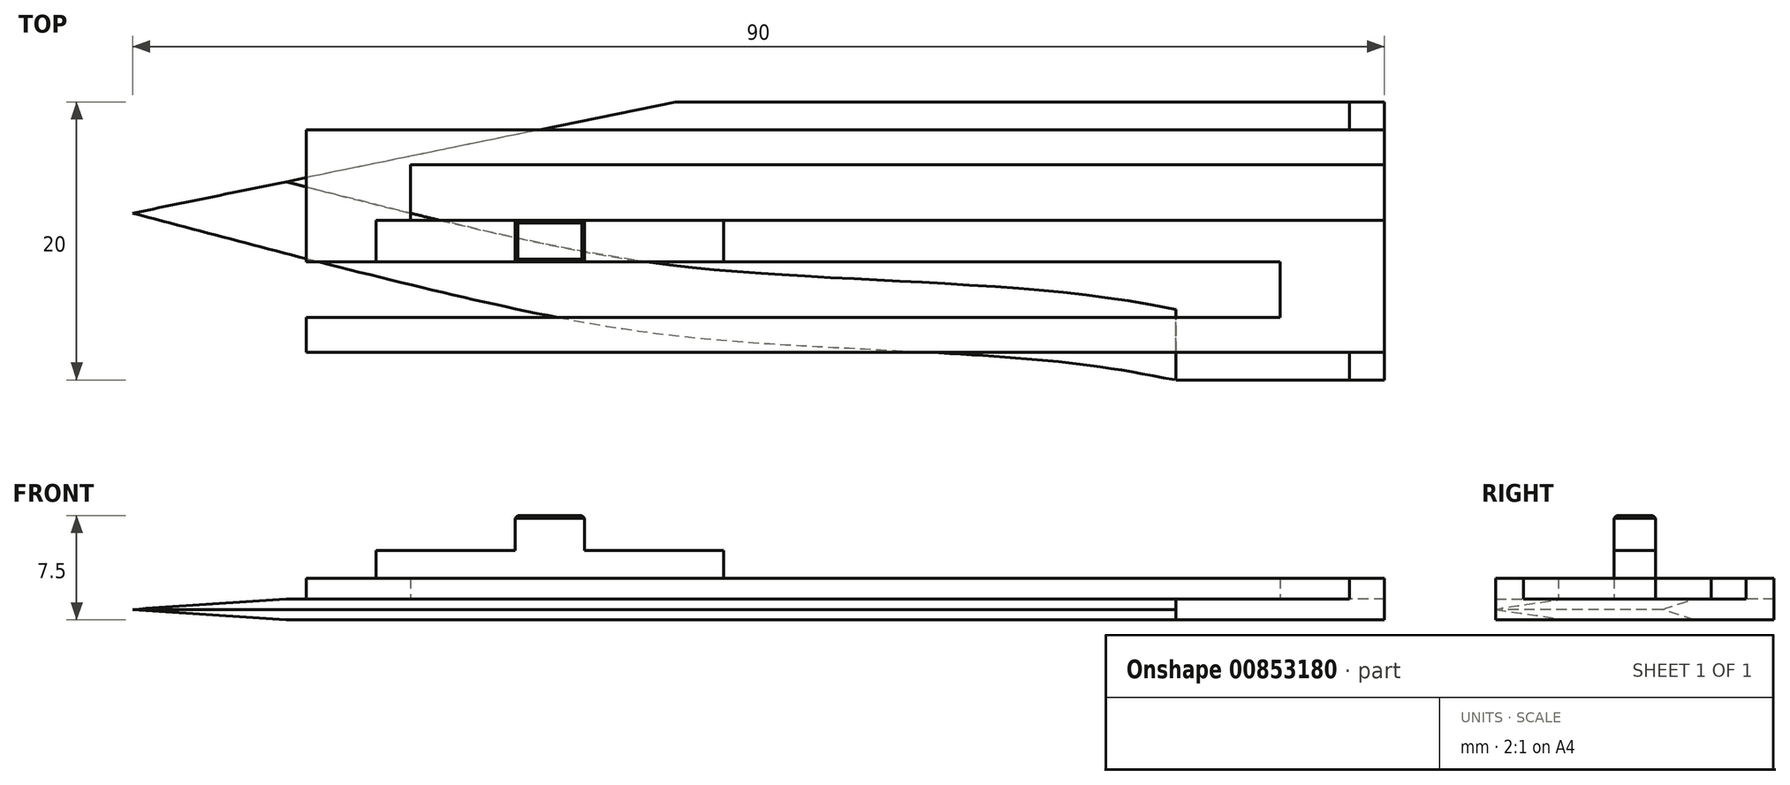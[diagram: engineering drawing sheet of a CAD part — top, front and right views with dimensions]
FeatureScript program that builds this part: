
annotation { "Feature Type Name" : "Feature", "Feature Type Description" : "" }
export const myFeature = defineFeature(function(context is Context, id is Id, definition is map)
    precondition{}
    {
        {
            var Q0;
            Q0=qCreatedBy(makeId("Top.planeOp"),FACE);
            var sketch = newSketch(context, id + "F0", { "sketchPlane" : qUnion([Q0])});
            skLineSegment(sketch, "E0.bottom", {"start": v(45, 10) * mm, "end": v(-5.97, 10) * mm});
            skLineSegment(sketch, "E0.left", {"start": v(45, 10) * mm, "end": v(45, -10) * mm});
            skPoint(sketch, "E0.middle", {"position": v(0, 0) * mm});
            skLineSegment(sketch, "E1", {"start": v(-5.97, 10) * mm, "end": v(-45, 2) * mm});
            skPoint(sketch, "E2.orphan", {"position": v(-45, 10) * mm});
            skPoint(sketch, "E0.top.end.orphan", {"position": v(-45, -10) * mm});
            skLineSegment(sketch, "E3", {"start": v(45, -10) * mm, "end": v(30, -10) * mm});
            skLineSegment(sketch, "E4", {"start": v(30, -10) * mm, "end": v(30, 10) * mm});
            skFitSpline(sketch, "E5", {"points": [v(-45, 2) * mm, v(-13.69, -5.63) * mm, v(2.33, -7.47) * mm, v(21.39, -8.67) * mm, v(30, -10) * mm], "startDerivative": vector(102.97, -27.22) * mm, "endDerivative": vector(43.54, -8.37) * mm});
            skSolve(sketch);
        }
        {
            var Q0;
            Q0 = qSketchRegion(id + "F0", true);
            extrude(context, id + "F1", {"entities" : qUnion([Q0]), "endBound" : BoundingType.SYMMETRIC, "depth" : 1.5 * mm, "offsetDistance" : 25 * mm});
        }
        {
            var Q0;
            Q0=makeQuery(id+"F1.opExtrude","CAP_EDGE",EDGE,{"disambiguationData":[OSD([sQuery(id+"F0.wireOp",EDGE,"E5")])],"isStart":false});
            var Q1;
            Q1=makeQuery(id+"F1.opExtrude","CAP_EDGE",EDGE,{"disambiguationData":[OSD([sQuery(id+"F0.wireOp",EDGE,"E5")])],"isStart":true});
            chamfer(context, id + "F2", {"entities" : qUnion([Q0, Q1]), "chamferType" : ChamferType.TWO_OFFSETS, "width1" : 5 * mm, "oppositeDirection" : false, "width2" : (1.5 / 2) * mm, "tangentPropagation" : true});
        }
        {
            var Q0;
            {var subQ0=sQuery(id+"F0.wireOp",EDGE,"E0.left");Q0=makeQuery(id+"F0.imprint","IMPRINT",FACE,{"disambiguationData":[TD([[makeQuery(id+"F0.imprint","IMPRINT",EDGE,{"derivedFrom":subQ0}),-1.0]])]});}
            extrude(context, id + "F3", {"entities" : qUnion([Q0]), "operationType" : NewBodyOperationType.ADD, "endBound" : BoundingType.SYMMETRIC, "depth" : 1.5 * mm, "offsetDistance" : 25 * mm});
        }
        {
            var Q0;
            {var subQ0=sQuery(id+"F0.wireOp",EDGE,"E3");var subQ1=sQuery(id+"F0.wireOp",EDGE,"E0.left");var subQ2=sQuery(id+"F0.wireOp",EDGE,"E0.bottom");Q0=makeQuery(id+"F3.boolean.opBoolean","MERGE",FACE,{"derivedFrom":[makeQuery(id+"F1.opExtrude","CAP_FACE",FACE,{"disambiguationData":[OSD([subQ2,subQ1,sQuery(id+"F0.wireOp",EDGE,"E1"),subQ0,sQuery(id+"F0.wireOp",EDGE,"E5")])],"isStart":false}),makeQuery(id+"F3.opExtrude","CAP_FACE",FACE,{"disambiguationData":[OSD([subQ2,subQ1,subQ0,sQuery(id+"F0.wireOp",EDGE,"E4")])],"isStart":false})]});}
            var sketch = newSketch(context, id + "F4", { "sketchPlane" : qUnion([Q0])});
            skLineSegment(sketch, "E6.bottom", {"start": v(45, -10) * mm, "end": v(42.5, -10) * mm});
            skLineSegment(sketch, "E6.top", {"start": v(45, -8) * mm, "end": v(42.5, -8) * mm});
            skLineSegment(sketch, "E6.left", {"start": v(45, -10) * mm, "end": v(45, -8) * mm});
            skLineSegment(sketch, "E6.right", {"start": v(42.5, -10) * mm, "end": v(42.5, -8) * mm});
            skLineSegment(sketch, "E7.bottom", {"start": v(45, 10) * mm, "end": v(42.5, 10) * mm});
            skLineSegment(sketch, "E7.top", {"start": v(45, 8) * mm, "end": v(42.5, 8) * mm});
            skLineSegment(sketch, "E7.left", {"start": v(45, 10) * mm, "end": v(45, 8) * mm});
            skLineSegment(sketch, "E7.right", {"start": v(42.5, 10) * mm, "end": v(42.5, 8) * mm});
            skSolve(sketch);
        }
        {
            var Q0;
            Q0 = qSketchRegion(id + "F4", true);
            extrude(context, id + "F5", {"entities" : qUnion([Q0]), "operationType" : NewBodyOperationType.ADD, "depth" : 1.5 * mm, "offsetDistance" : 25 * mm});
        }
        {
            var Q0;
            {var subQ0=sQuery(id+"F0.wireOp",EDGE,"E3");var subQ1=sQuery(id+"F0.wireOp",EDGE,"E0.left");var subQ2=sQuery(id+"F0.wireOp",EDGE,"E0.bottom");Q0=makeQuery(id+"F3.boolean.opBoolean","MERGE",FACE,{"derivedFrom":[makeQuery(id+"F1.opExtrude","CAP_FACE",FACE,{"disambiguationData":[OSD([subQ2,subQ1,sQuery(id+"F0.wireOp",EDGE,"E1"),subQ0,sQuery(id+"F0.wireOp",EDGE,"E5")])],"isStart":false}),makeQuery(id+"F3.opExtrude","CAP_FACE",FACE,{"disambiguationData":[OSD([subQ2,subQ1,subQ0,sQuery(id+"F0.wireOp",EDGE,"E4")])],"isStart":false})]});}
            var sketch = newSketch(context, id + "F6", { "sketchPlane" : qUnion([Q0])});
            skPoint(sketch, "E8.right.end.orphan", {"position": v(-102.5, -2) * mm});
            skPoint(sketch, "E8.right.start.orphan", {"position": v(-102.5, 2) * mm});
            skLineSegment(sketch, "E9", {"start": v(45, 8) * mm, "end": v(-32.5, 8) * mm});
            skPoint(sketch, "E9.endSnap0", {"position": v(-19.97, 8) * mm});
            skLineSegment(sketch, "E10", {"start": v(-32.5, 8) * mm, "end": v(-32.5, -1.5) * mm});
            skLineSegment(sketch, "E11", {"start": v(-32.5, -1.5) * mm, "end": v(37.5, -1.5) * mm});
            skLineSegment(sketch, "E12", {"start": v(37.5, -1.5) * mm, "end": v(37.5, -5.5) * mm});
            skLineSegment(sketch, "E13", {"start": v(37.5, -5.5) * mm, "end": v(-32.5, -5.5) * mm});
            skLineSegment(sketch, "E14", {"start": v(-32.5, -5.5) * mm, "end": v(-32.5, -8) * mm});
            skLineSegment(sketch, "E15", {"start": v(-32.5, -8) * mm, "end": v(45, -8) * mm});
            skLineSegment(sketch, "E16", {"start": v(45, -8) * mm, "end": v(45, 1.5) * mm});
            skLineSegment(sketch, "E17", {"start": v(45, 1.5) * mm, "end": v(-25, 1.5) * mm});
            skLineSegment(sketch, "E18", {"start": v(-25, 1.5) * mm, "end": v(-25, 5.5) * mm});
            skLineSegment(sketch, "E19", {"start": v(-25, 5.5) * mm, "end": v(45, 5.5) * mm});
            skLineSegment(sketch, "E20", {"start": v(45, 5.5) * mm, "end": v(45, 8) * mm});
            skSolve(sketch);
        }
        {
            var Q0;
            Q0 = qSketchRegion(id + "F6", true);
            extrude(context, id + "F7", {"entities" : qUnion([Q0]), "depth" : 1.5 * mm, "offsetDistance" : 25 * mm});
        }
        {
            var Q0;
            Q0=makeQuery(id+"F7.opExtrude","CAP_FACE",FACE,{"disambiguationData":[OSD([sQuery(id+"F6.wireOp",EDGE,"E9"),sQuery(id+"F6.wireOp",EDGE,"E10"),sQuery(id+"F6.wireOp",EDGE,"E11"),sQuery(id+"F6.wireOp",EDGE,"E12"),sQuery(id+"F6.wireOp",EDGE,"E13"),sQuery(id+"F6.wireOp",EDGE,"E14"),sQuery(id+"F6.wireOp",EDGE,"E15"),sQuery(id+"F6.wireOp",EDGE,"E16"),sQuery(id+"F6.wireOp",EDGE,"E17"),sQuery(id+"F6.wireOp",EDGE,"E18"),sQuery(id+"F6.wireOp",EDGE,"E19"),sQuery(id+"F6.wireOp",EDGE,"E20")])],"isStart":false});
            var sketch = newSketch(context, id + "F8", { "sketchPlane" : qUnion([Q0])});
            skLineSegment(sketch, "E21.bottom", {"start": v(-2.5, 1.5) * mm, "end": v(-27.5, 1.5) * mm});
            skLineSegment(sketch, "E21.top", {"start": v(-2.5, -1.5) * mm, "end": v(-27.5, -1.5) * mm});
            skLineSegment(sketch, "E21.left", {"start": v(-2.5, 1.5) * mm, "end": v(-2.5, -1.5) * mm});
            skLineSegment(sketch, "E21.right", {"start": v(-27.5, 1.5) * mm, "end": v(-27.5, -1.5) * mm});
            skSolve(sketch);
        }
        {
            var Q0;
            Q0 = qSketchRegion(id + "F8", true);
            extrude(context, id + "F9", {"entities" : qUnion([Q0]), "operationType" : NewBodyOperationType.ADD, "depth" : 2 * mm, "offsetDistance" : 25 * mm});
        }
        {
            var Q0;
            Q0=makeQuery(id+"F9.opExtrude","CAP_FACE",FACE,{"disambiguationData":[OSD([sQuery(id+"F8.wireOp",EDGE,"E21.bottom"),sQuery(id+"F8.wireOp",EDGE,"E21.top"),sQuery(id+"F8.wireOp",EDGE,"E21.left"),sQuery(id+"F8.wireOp",EDGE,"E21.right")])],"isStart":false});
            var sketch = newSketch(context, id + "F10", { "sketchPlane" : qUnion([Q0])});
            skLineSegment(sketch, "E22.bottom", {"start": v(-17.5, 1.5) * mm, "end": v(-12.5, 1.5) * mm});
            skLineSegment(sketch, "E22.top", {"start": v(-17.5, -1.5) * mm, "end": v(-12.5, -1.5) * mm});
            skLineSegment(sketch, "E22.left", {"start": v(-17.5, 1.5) * mm, "end": v(-17.5, -1.5) * mm});
            skLineSegment(sketch, "E22.right", {"start": v(-12.5, 1.5) * mm, "end": v(-12.5, -1.5) * mm});
            skSolve(sketch);
        }
        {
            var Q0;
            Q0 = qSketchRegion(id + "F10", true);
            extrude(context, id + "F11", {"entities" : qUnion([Q0]), "operationType" : NewBodyOperationType.ADD, "depth" : 2.5 * mm, "offsetDistance" : 25 * mm});
        }
        {
            var Q0;
            Q0=makeQuery(id+"F11.opExtrude","CAP_EDGE",EDGE,{"disambiguationData":[OSD([sQuery(id+"F10.wireOp",EDGE,"E22.left")])],"isStart":false});
            var Q1;
            Q1=makeQuery(id+"F11.opExtrude","CAP_EDGE",EDGE,{"disambiguationData":[OSD([sQuery(id+"F10.wireOp",EDGE,"E22.right")])],"isStart":false});
            var Q2;
            Q2=makeQuery(id+"F11.opExtrude","CAP_EDGE",EDGE,{"disambiguationData":[OSD([sQuery(id+"F10.wireOp",EDGE,"E22.top")])],"isStart":false});
            var Q3;
            Q3=makeQuery(id+"F11.opExtrude","CAP_EDGE",EDGE,{"disambiguationData":[OSD([sQuery(id+"F10.wireOp",EDGE,"E22.bottom")])],"isStart":false});
            chamfer(context, id + "F12", {"entities" : qUnion([Q0, Q1, Q2, Q3]), "width" : 0.2 * mm, "tangentPropagation" : true});
        }
    });
